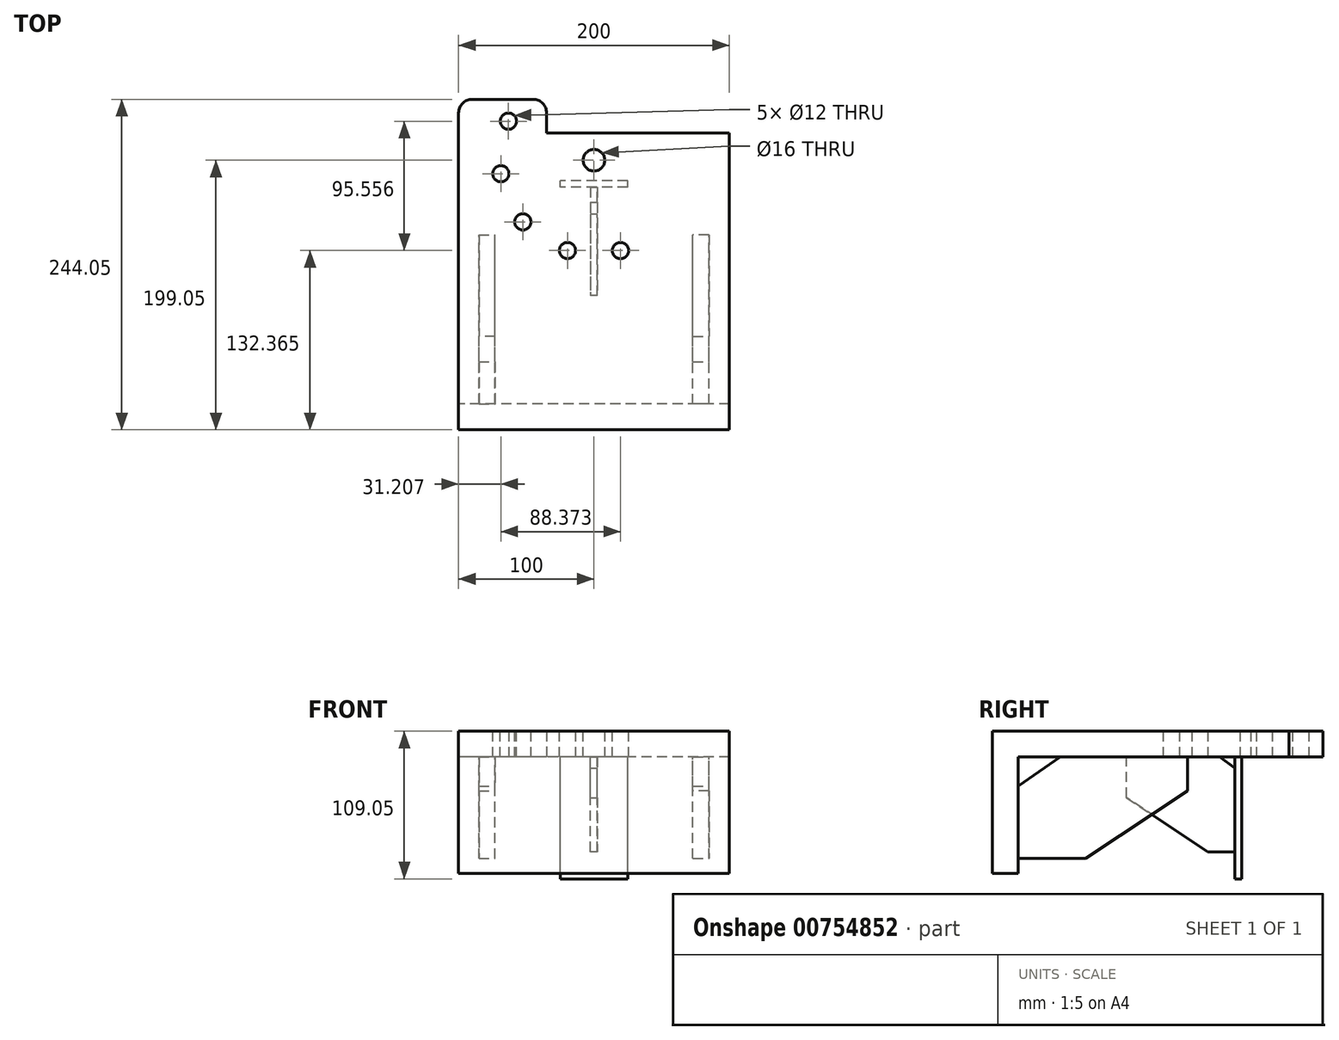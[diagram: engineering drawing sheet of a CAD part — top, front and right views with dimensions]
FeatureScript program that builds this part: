
annotation { "Feature Type Name" : "Feature", "Feature Type Description" : "" }
export const myFeature = defineFeature(function(context is Context, id is Id, definition is map)
    precondition{}
    {
        {
            var Q0;
            Q0=qCreatedBy(makeId("Top.planeOp"),FACE);
            var sketch = newSketch(context, id + "F0", { "sketchPlane" : qUnion([Q0])});
            skLineSegment(sketch, "E0.bottom", {"start": v(100, 100) * mm, "end": v(-100, 100) * mm});
            skLineSegment(sketch, "E0.top", {"start": v(100, -100) * mm, "end": v(-100, -100) * mm});
            skLineSegment(sketch, "E0.left", {"start": v(100, 100) * mm, "end": v(100, -100) * mm});
            skLineSegment(sketch, "E0.right", {"start": v(-100, 100) * mm, "end": v(-100, -100) * mm});
            skPoint(sketch, "E0.middle", {"position": v(0, 0) * mm});
            skSolve(sketch);
        }
        {
            var Q0;
            Q0=makeQuery(id+"F0.imprint","IMPRINT",FACE,{"disambiguationData":[TD([[makeQuery(id+"F0.imprint","IMPRINT",EDGE,{"derivedFrom":sQuery(id+"F0.wireOp",EDGE,"E0.bottom")}),1.0]])]});
            extrude(context, id + "F1", {"entities" : qUnion([Q0]), "depth" : 19.05 * mm, "offsetDistance" : 25 * mm});
        }
        {
            var Q0;
            Q0=makeQuery(id+"F1.opExtrude","CAP_FACE",FACE,{"disambiguationData":[OSD([sQuery(id+"F0.wireOp",EDGE,"E0.bottom"),sQuery(id+"F0.wireOp",EDGE,"E0.top"),sQuery(id+"F0.wireOp",EDGE,"E0.left"),sQuery(id+"F0.wireOp",EDGE,"E0.right")])],"isStart":false});
            var sketch = newSketch(context, id + "F2", { "sketchPlane" : qUnion([Q0])});
            skPoint(sketch, "E1", {"position": v(0, 80) * mm});
            skSolve(sketch);
        }
        {
            var Q0;
            Q0=sQuery(id+"F2.wireOp",VERTEX,"E1");
            var Q1;
            Q1=makeQuery(id+"F1.opExtrude","SWEPT_BODY",BODY,{"disambiguationData":[OSD([sQuery(id+"F0.wireOp",EDGE,"E0.bottom"),sQuery(id+"F0.wireOp",EDGE,"E0.top"),sQuery(id+"F0.wireOp",EDGE,"E0.left"),sQuery(id+"F0.wireOp",EDGE,"E0.right")])]});
            hole(context, id + "F3", {"style" : HoleStyle.SIMPLE, "endStyle" : HoleEndStyle.THROUGH, "standardTappedOrClearance" : lookupTablePath({ "standard" : "ISO", "size" : "16", "type" : "Drilled" }), "standardBlindInLast" : lookupTablePath({ "standard" : "ISO", "size" : "16", "type" : "Drilled" }), "holeDiameter" : 16 * mm, "majorDiameter" : 10 * mm, "isTappedThrough" : true, "tappedDepth" : 12 * mm, "tapClearance" : 3, "locations" : qUnion([Q0]), "scope" : qUnion([Q1])});
        }
        {
            var Q0;
            Q0=makeQuery(id+"F1.opExtrude","CAP_FACE",FACE,{"disambiguationData":[OSD([sQuery(id+"F0.wireOp",EDGE,"E0.bottom"),sQuery(id+"F0.wireOp",EDGE,"E0.top"),sQuery(id+"F0.wireOp",EDGE,"E0.left"),sQuery(id+"F0.wireOp",EDGE,"E0.right")])],"isStart":true});
            var sketch = newSketch(context, id + "F4", { "sketchPlane" : qUnion([Q0])});
            skLineSegment(sketch, "E2.bottom", {"start": v(85, 100) * mm, "end": v(73, 100) * mm});
            skLineSegment(sketch, "E2.top", {"start": v(85, -25) * mm, "end": v(73, -25) * mm});
            skLineSegment(sketch, "E2.left", {"start": v(85, 100) * mm, "end": v(85, -25) * mm});
            skLineSegment(sketch, "E2.right", {"start": v(73, 100) * mm, "end": v(73, -25) * mm});
            skSolve(sketch);
        }
        {
            var Q0;
            Q0=makeQuery(id+"F4.imprint","IMPRINT",FACE,{"disambiguationData":[TD([[makeQuery(id+"F4.imprint","IMPRINT",EDGE,{"derivedFrom":sQuery(id+"F4.wireOp",EDGE,"E2.bottom")}),1.0]])]});
            extrude(context, id + "F5", {"entities" : qUnion([Q0]), "depth" : 75 * mm, "offsetDistance" : 25 * mm});
        }
        {
            var Q0;
            Q0=makeQuery(id+"F5.opExtrude","CAP_EDGE",EDGE,{"disambiguationData":[OSD([sQuery(id+"F4.wireOp",EDGE,"E2.top")])],"isStart":false});
            chamfer(context, id + "F6", {"entities" : qUnion([Q0]), "chamferType" : ChamferType.TWO_OFFSETS, "width1" : 50 * mm, "oppositeDirection" : false, "width2" : 75 * mm, "tangentPropagation" : true});
        }
        {
            var Q0;
            Q0=makeQuery(id+"F5.opExtrude","SWEPT_BODY",BODY,{"disambiguationData":[OSD([sQuery(id+"F4.wireOp",EDGE,"E2.bottom"),sQuery(id+"F4.wireOp",EDGE,"E2.top"),sQuery(id+"F4.wireOp",EDGE,"E2.left"),sQuery(id+"F4.wireOp",EDGE,"E2.right")])]});
            var Q1;
            Q1=qCreatedBy(makeId("Right.planeOp"),FACE);
            mirror(context, id + "F7", {"operationType" : NewBodyOperationType.ADD, "entities" : qUnion([Q0]), "mirrorPlane" : qUnion([Q1])});
        }
        {
            var Q0;
            {var subQ0=makeQuery(id+"F5.opExtrude","SWEPT_FACE",FACE,{"disambiguationData":[OSD([sQuery(id+"F4.wireOp",EDGE,"E2.bottom")])]});Q0=makeQuery(id+"F7.boolean.opBoolean","MERGE",FACE,{"derivedFrom":[makeQuery(id+"F1.opExtrude","SWEPT_FACE",FACE,{"disambiguationData":[OSD([sQuery(id+"F0.wireOp",EDGE,"E0.top")])]}),subQ0,makeQuery(id+"F7.opPattern","COPY",FACE,{"derivedFrom":subQ0,"instanceName":"1"})]});}
            var sketch = newSketch(context, id + "F8", { "sketchPlane" : qUnion([Q0])});
            skLineSegment(sketch, "E3.bottom", {"start": v(100, 19.05) * mm, "end": v(-100, 19.05) * mm});
            skLineSegment(sketch, "E3.top", {"start": v(100, -85.95) * mm, "end": v(-100, -85.95) * mm});
            skLineSegment(sketch, "E3.left", {"start": v(100, 19.05) * mm, "end": v(100, -85.95) * mm});
            skLineSegment(sketch, "E3.right", {"start": v(-100, 19.05) * mm, "end": v(-100, -85.95) * mm});
            skSolve(sketch);
        }
        {
            var Q0;
            {var subQ16=sQuery(id+"F8.wireOp",EDGE,"E3.top");Q0=makeQuery(id+"F8.imprint","IMPRINT",FACE,{"disambiguationData":[TD([[makeQuery(id+"F8.imprint","IMPRINT",EDGE,{"derivedFrom":subQ16}),-1.0]])]});}
            var Q1;
            {var subQ0=sQuery(id+"F8.wireOp",EDGE,"E3.bottom");Q1=makeQuery(id+"F8.imprint","IMPRINT",FACE,{"disambiguationData":[TD([[makeQuery(id+"F8.imprint","IMPRINT",EDGE,{"derivedFrom":subQ0}),1.0]])]});}
            var Q2;
            {var subQ3=sQuery(id+"F0.wireOp",EDGE,"E0.top");var subQ17=makeQuery(id+"F1.opExtrude","CAP_EDGE",EDGE,{"disambiguationData":[OSD([subQ3])],"isStart":false});Q2=makeQuery(id+"F8.imprint","IMPRINT",FACE,{"disambiguationData":[TD([[makeQuery(id+"F8.imprint","IMPRINT",EDGE,{"derivedFrom":subQ17}),1.0]])]});}
            extrude(context, id + "F9", {"entities" : qUnion([Q0, Q1, Q2]), "operationType" : NewBodyOperationType.ADD, "depth" : 19.05 * mm, "offsetDistance" : 25 * mm});
        }
        {
            var Q0;
            Q0=makeQuery(id+"F5.opExtrude","SWEPT_FACE",FACE,{"disambiguationData":[OSD([sQuery(id+"F4.wireOp",EDGE,"E2.left")])]});
            var sketch = newSketch(context, id + "F10", { "sketchPlane" : qUnion([Q0])});
            skLineSegment(sketch, "E4", {"start": v(-100, -21.65) * mm, "end": v(-68.82, 0) * mm});
            skSolve(sketch);
        }
        {
            var Q0;
            {var subQ0=sQuery(id+"F10.wireOp",EDGE,"E4");Q0=makeQuery(id+"F10.imprint","IMPRINT",FACE,{"disambiguationData":[TD([[makeQuery(id+"F10.imprint","IMPRINT",EDGE,{"derivedFrom":subQ0}),1.0]])]});}
            extrude(context, id + "F11", {"entities" : qUnion([Q0]), "operationType" : NewBodyOperationType.REMOVE, "oppositeDirection" : true, "depth" : 500 * mm, "offsetDistance" : 25 * mm});
        }
        {
            var Q0;
            Q0=makeQuery(id+"F11.boolean.opBoolean","MERGE",FACE,{"derivedFrom":[makeQuery(id+"F1.opExtrude","CAP_FACE",FACE,{"disambiguationData":[OSD([sQuery(id+"F0.wireOp",EDGE,"E0.bottom"),sQuery(id+"F0.wireOp",EDGE,"E0.top"),sQuery(id+"F0.wireOp",EDGE,"E0.left"),sQuery(id+"F0.wireOp",EDGE,"E0.right")])],"isStart":true})],"fromTools":[makeQuery(id+"F11.opExtrude","SWEPT_FACE",FACE,{"disambiguationData":[OSD([sQuery(id+"F4.wireOp",EDGE,"E2.left")])]})]});
            var sketch = newSketch(context, id + "F12", { "sketchPlane" : qUnion([Q0])});
            skLineSegment(sketch, "E5.bottom", {"start": v(25, -60) * mm, "end": v(-25, -60) * mm});
            skLineSegment(sketch, "E5.top", {"start": v(25, -65) * mm, "end": v(-25, -65) * mm});
            skLineSegment(sketch, "E5.left", {"start": v(25, -60) * mm, "end": v(25, -65) * mm});
            skLineSegment(sketch, "E5.right", {"start": v(-25, -60) * mm, "end": v(-25, -65) * mm});
            skSolve(sketch);
        }
        {
            var Q0;
            Q0=makeQuery(id+"F12.imprint","IMPRINT",FACE,{"disambiguationData":[TD([[makeQuery(id+"F12.imprint","IMPRINT",EDGE,{"derivedFrom":sQuery(id+"F12.wireOp",EDGE,"E5.bottom")}),1.0]])]});
            extrude(context, id + "F13", {"entities" : qUnion([Q0]), "operationType" : NewBodyOperationType.ADD, "depth" : 90 * mm, "offsetDistance" : 25 * mm});
        }
        {
            var Q0;
            Q0=makeQuery(id+"F11.boolean.opBoolean","MERGE",FACE,{"derivedFrom":[makeQuery(id+"F1.opExtrude","CAP_FACE",FACE,{"disambiguationData":[OSD([sQuery(id+"F0.wireOp",EDGE,"E0.bottom"),sQuery(id+"F0.wireOp",EDGE,"E0.top"),sQuery(id+"F0.wireOp",EDGE,"E0.left"),sQuery(id+"F0.wireOp",EDGE,"E0.right")])],"isStart":true})],"fromTools":[makeQuery(id+"F11.opExtrude","SWEPT_FACE",FACE,{"disambiguationData":[OSD([sQuery(id+"F4.wireOp",EDGE,"E2.left")])]})]});
            var sketch = newSketch(context, id + "F14", { "sketchPlane" : qUnion([Q0])});
            skLineSegment(sketch, "E6.bottom", {"start": v(2.5, -60) * mm, "end": v(-2.5, -60) * mm});
            skLineSegment(sketch, "E6.top", {"start": v(2.5, 20) * mm, "end": v(-2.5, 20) * mm});
            skLineSegment(sketch, "E6.left", {"start": v(2.5, -60) * mm, "end": v(2.5, 20) * mm});
            skLineSegment(sketch, "E6.right", {"start": v(-2.5, -60) * mm, "end": v(-2.5, 20) * mm});
            skSolve(sketch);
        }
        {
            var Q0;
            Q0=makeQuery(id+"F14.imprint","IMPRINT",FACE,{"disambiguationData":[TD([[makeQuery(id+"F14.imprint","IMPRINT",EDGE,{"derivedFrom":sQuery(id+"F14.wireOp",EDGE,"E6.bottom")}),-1.0]])]});
            extrude(context, id + "F15", {"entities" : qUnion([Q0]), "operationType" : NewBodyOperationType.ADD, "depth" : 70 * mm, "offsetDistance" : 25 * mm});
        }
        {
            var Q0;
            Q0=makeQuery(id+"F15.opExtrude","CAP_EDGE",EDGE,{"disambiguationData":[OSD([sQuery(id+"F14.wireOp",EDGE,"E6.top")])],"isStart":false});
            chamfer(context, id + "F16", {"entities" : qUnion([Q0]), "chamferType" : ChamferType.TWO_OFFSETS, "width1" : 60 * mm, "oppositeDirection" : false, "width2" : 40 * mm, "tangentPropagation" : true});
        }
        {
            var Q0;
            Q0=makeQuery(id+"F15.opExtrude","SWEPT_FACE",FACE,{"disambiguationData":[OSD([sQuery(id+"F14.wireOp",EDGE,"E6.left")])]});
            var sketch = newSketch(context, id + "F17", { "sketchPlane" : qUnion([Q0])});
            skLineSegment(sketch, "E7", {"start": v(49.05, 0) * mm, "end": v(60, -8.05) * mm});
            skSolve(sketch);
        }
        {
            var Q0;
            {var subQ0=sQuery(id+"F17.wireOp",EDGE,"E7");Q0=makeQuery(id+"F17.imprint","IMPRINT",FACE,{"disambiguationData":[TD([[makeQuery(id+"F17.imprint","IMPRINT",EDGE,{"derivedFrom":subQ0}),1.0]])]});}
            extrude(context, id + "F18", {"entities" : qUnion([Q0]), "operationType" : NewBodyOperationType.REMOVE, "oppositeDirection" : true, "depth" : 25 * mm, "offsetDistance" : 25 * mm});
        }
        {
            var Q0;
            Q0=makeQuery(id+"F1.opExtrude","SWEPT_FACE",FACE,{"disambiguationData":[OSD([sQuery(id+"F0.wireOp",EDGE,"E0.bottom")])]});
            var sketch = newSketch(context, id + "F19", { "sketchPlane" : qUnion([Q0])});
            skLineSegment(sketch, "E8.bottom", {"start": v(100, 19.05) * mm, "end": v(35, 19.05) * mm});
            skLineSegment(sketch, "E8.top", {"start": v(100, 0) * mm, "end": v(35, 0) * mm});
            skLineSegment(sketch, "E8.left", {"start": v(100, 19.05) * mm, "end": v(100, 0) * mm});
            skLineSegment(sketch, "E8.right", {"start": v(35, 19.05) * mm, "end": v(35, 0) * mm});
            skSolve(sketch);
        }
        {
            var Q0;
            Q0=makeQuery(id+"F19.imprint","IMPRINT",FACE,{"disambiguationData":[TD([[makeQuery(id+"F19.imprint","IMPRINT",EDGE,{"derivedFrom":sQuery(id+"F19.wireOp",EDGE,"E8.bottom")}),-1.0]])]});
            extrude(context, id + "F20", {"entities" : qUnion([Q0]), "operationType" : NewBodyOperationType.ADD, "depth" : 25 * mm, "offsetDistance" : 25 * mm});
        }
        {
            var Q0;
            Q0=makeQuery(id+"F20.opExtrude","CAP_EDGE",EDGE,{"disambiguationData":[OSD([sQuery(id+"F19.wireOp",EDGE,"E8.left")])],"isStart":false});
            var Q1;
            Q1=makeQuery(id+"F20.opExtrude","CAP_EDGE",EDGE,{"disambiguationData":[OSD([sQuery(id+"F19.wireOp",EDGE,"E8.right")])],"isStart":false});
            var Q2;
            Q2=makeQuery(id+"F20.opExtrude","CAP_EDGE",EDGE,{"disambiguationData":[OSD([sQuery(id+"F19.wireOp",EDGE,"E8.right")])],"isStart":true});
            fillet(context, id + "F21", {"entities" : qUnion([Q0, Q1, Q2]), "radius" : 10 * mm, "tangentPropagation" : true, "allowEdgeOverflow" : false});
        }
        {
            var Q0;
            Q0=makeQuery(id+"F20.boolean.opBoolean","MERGE",FACE,{"derivedFrom":[makeQuery(id+"F9.boolean.opBoolean","MERGE",FACE,{"derivedFrom":[makeQuery(id+"F1.opExtrude","CAP_FACE",FACE,{"disambiguationData":[OSD([sQuery(id+"F0.wireOp",EDGE,"E0.bottom"),sQuery(id+"F0.wireOp",EDGE,"E0.top"),sQuery(id+"F0.wireOp",EDGE,"E0.left"),sQuery(id+"F0.wireOp",EDGE,"E0.right")])],"isStart":false}),makeQuery(id+"F9.opExtrude","SWEPT_FACE",FACE,{"disambiguationData":[OSD([sQuery(id+"F8.wireOp",EDGE,"E3.bottom")])]})]}),makeQuery(id+"F20.opExtrude","SWEPT_FACE",FACE,{"disambiguationData":[OSD([sQuery(id+"F19.wireOp",EDGE,"E8.bottom")])]})]});
            var sketch = newSketch(context, id + "F22", { "sketchPlane" : qUnion([Q0])});
            skCircle(sketch, "E9", {"center": v(-63.22, 108.87) * mm, "radius": 6 * mm});
            skCircle(sketch, "E10.1.0", {"center": v(-68.8, 70.1) * mm, "radius": 6 * mm});
            skCircle(sketch, "E10.2.0", {"center": v(-52.52, 34.49) * mm, "radius": 6 * mm});
            skPoint(sketch, "E10.center", {"position": v(0, 80) * mm});
            skCircle(sketch, "E11.1.3.0", {"center": v(-19.58, 13.32) * mm, "radius": 6 * mm});
            skCircle(sketch, "E11.1.4.0", {"center": v(19.58, 13.32) * mm, "radius": 6 * mm});
            skCircle(sketch, "E11.1.5.0", {"center": v(52.52, 34.49) * mm, "radius": 6 * mm});
            skCircle(sketch, "E11.1.6.0", {"center": v(68.8, 70.1) * mm, "radius": 6 * mm});
            skCircle(sketch, "E11.1.7.0", {"center": v(63.22, 108.87) * mm, "radius": 6 * mm});
            skCircle(sketch, "E11.1.8.0", {"center": v(37.57, 138.47) * mm, "radius": 6 * mm});
            skCircle(sketch, "E11.1.9.0", {"center": v(0, 149.5) * mm, "radius": 6 * mm});
            skCircle(sketch, "E11.1.10.0", {"center": v(-37.57, 138.47) * mm, "radius": 6 * mm});
            skSolve(sketch);
        }
        {
            var Q0;
            Q0=makeQuery(id+"F22.imprint","IMPRINT",FACE,{"disambiguationData":[TD([[makeQuery(id+"F22.imprint","IMPRINT",EDGE,{"derivedFrom":sQuery(id+"F22.wireOp",EDGE,"E9")}),1.0]])]});
            var Q1;
            Q1=makeQuery(id+"F22.imprint","IMPRINT",FACE,{"disambiguationData":[TD([[makeQuery(id+"F22.imprint","IMPRINT",EDGE,{"derivedFrom":sQuery(id+"F22.wireOp",EDGE,"E10.1.0")}),1.0]])]});
            var Q2;
            Q2=makeQuery(id+"F22.imprint","IMPRINT",FACE,{"disambiguationData":[TD([[makeQuery(id+"F22.imprint","IMPRINT",EDGE,{"derivedFrom":sQuery(id+"F22.wireOp",EDGE,"E10.2.0")}),1.0]])]});
            var Q3;
            Q3=makeQuery(id+"F22.imprint","IMPRINT",FACE,{"disambiguationData":[TD([[makeQuery(id+"F22.imprint","IMPRINT",EDGE,{"derivedFrom":sQuery(id+"F22.wireOp",EDGE,"E11.1.3.0")}),1.0]])]});
            var Q4;
            Q4=makeQuery(id+"F22.imprint","IMPRINT",FACE,{"disambiguationData":[TD([[makeQuery(id+"F22.imprint","IMPRINT",EDGE,{"derivedFrom":sQuery(id+"F22.wireOp",EDGE,"E11.1.4.0")}),1.0]])]});
            extrude(context, id + "F23", {"entities" : qUnion([Q0, Q1, Q2, Q3, Q4]), "operationType" : NewBodyOperationType.REMOVE, "oppositeDirection" : true, "depth" : 25 * mm, "offsetDistance" : 25 * mm});
        }
    });
